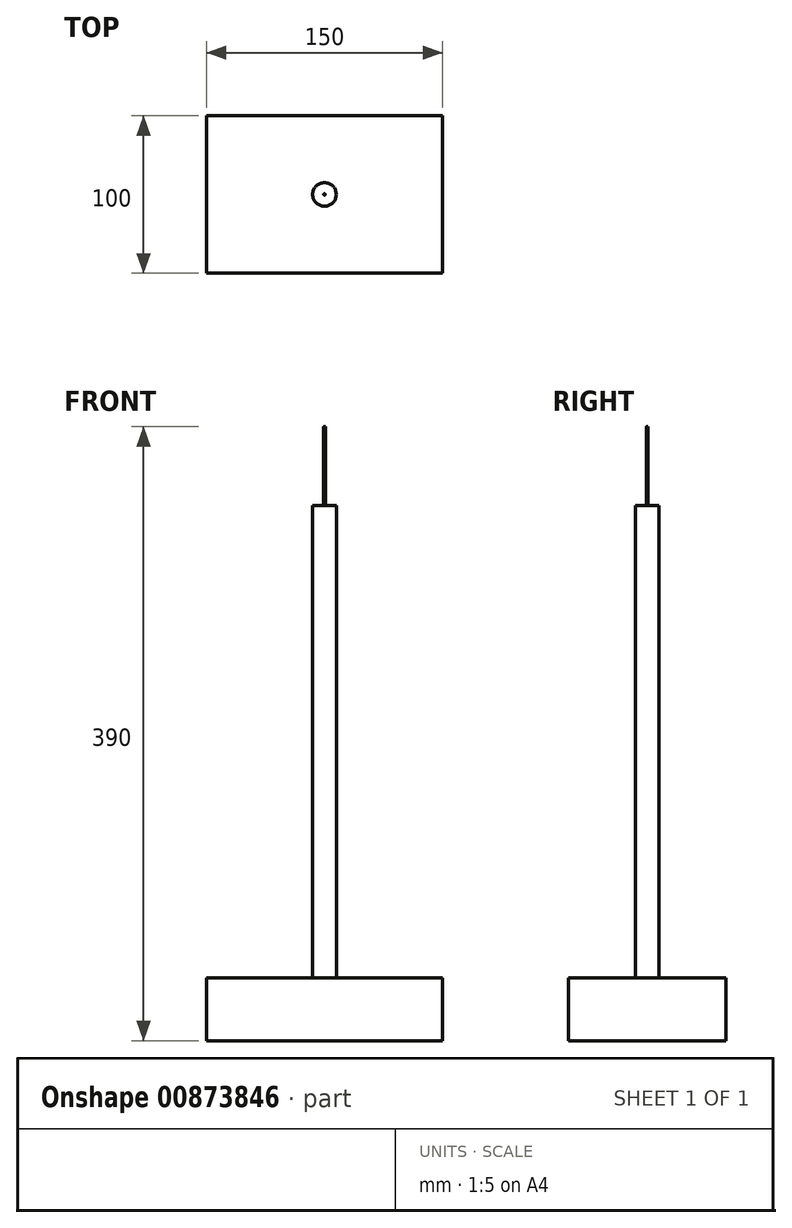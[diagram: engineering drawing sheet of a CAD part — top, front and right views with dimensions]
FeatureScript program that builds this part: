
annotation { "Feature Type Name" : "Feature", "Feature Type Description" : "" }
export const myFeature = defineFeature(function(context is Context, id is Id, definition is map)
    precondition{}
    {
        {
            var Q0;
            Q0=qCreatedBy(makeId("Top.planeOp"),FACE);
            var sketch = newSketch(context, id + "F0", { "sketchPlane" : qUnion([Q0])});
            skLineSegment(sketch, "E0.bottom", {"start": v(75, -50) * mm, "end": v(-75, -50) * mm});
            skLineSegment(sketch, "E0.top", {"start": v(75, 50) * mm, "end": v(-75, 50) * mm});
            skLineSegment(sketch, "E0.left", {"start": v(75, -50) * mm, "end": v(75, 50) * mm});
            skLineSegment(sketch, "E0.right", {"start": v(-75, -50) * mm, "end": v(-75, 50) * mm});
            skPoint(sketch, "E0.middle", {"position": v(0, 0) * mm});
            skSolve(sketch);
        }
        {
            var Q0;
            Q0=makeQuery(id+"F0.imprint","IMPRINT",FACE,{"disambiguationData":[TD([[makeQuery(id+"F0.imprint","IMPRINT",EDGE,{"derivedFrom":sQuery(id+"F0.wireOp",EDGE,"E0.bottom")}),-1.0]])]});
            extrude(context, id + "F1", {"entities" : qUnion([Q0]), "depth" : -40 * mm, "offsetDistance" : 25 * mm});
        }
        {
            var Q0;
            Q0=qCreatedBy(makeId("Top.planeOp"),FACE);
            var sketch = newSketch(context, id + "F2", { "sketchPlane" : qUnion([Q0])});
            skCircle(sketch, "E1", {"center": v(0, 0) * mm, "radius": 7.5 * mm});
            skCircle(sketch, "E2", {"center": v(0, 0) * mm, "radius": 0.5 * mm});
            skSolve(sketch);
        }
        {
            var Q0;
            Q0=makeQuery(id+"F2.imprint","IMPRINT",FACE,{"disambiguationData":[TD([[makeQuery(id+"F2.imprint","IMPRINT",EDGE,{"derivedFrom":sQuery(id+"F2.wireOp",EDGE,"E2")}),1.0]])]});
            extrude(context, id + "F3", {"entities" : qUnion([Q0]), "depth" : 350 * mm, "offsetDistance" : 25 * mm});
        }
        {
            var Q0;
            Q0=makeQuery(id+"F2.imprint","IMPRINT",FACE,{"disambiguationData":[TD([[makeQuery(id+"F2.imprint","IMPRINT",EDGE,{"derivedFrom":sQuery(id+"F2.wireOp",EDGE,"E1")}),1.0]])]});
            extrude(context, id + "F4", {"entities" : qUnion([Q0]), "operationType" : NewBodyOperationType.ADD, "depth" : 300 * mm, "offsetDistance" : 25 * mm});
        }
    });
